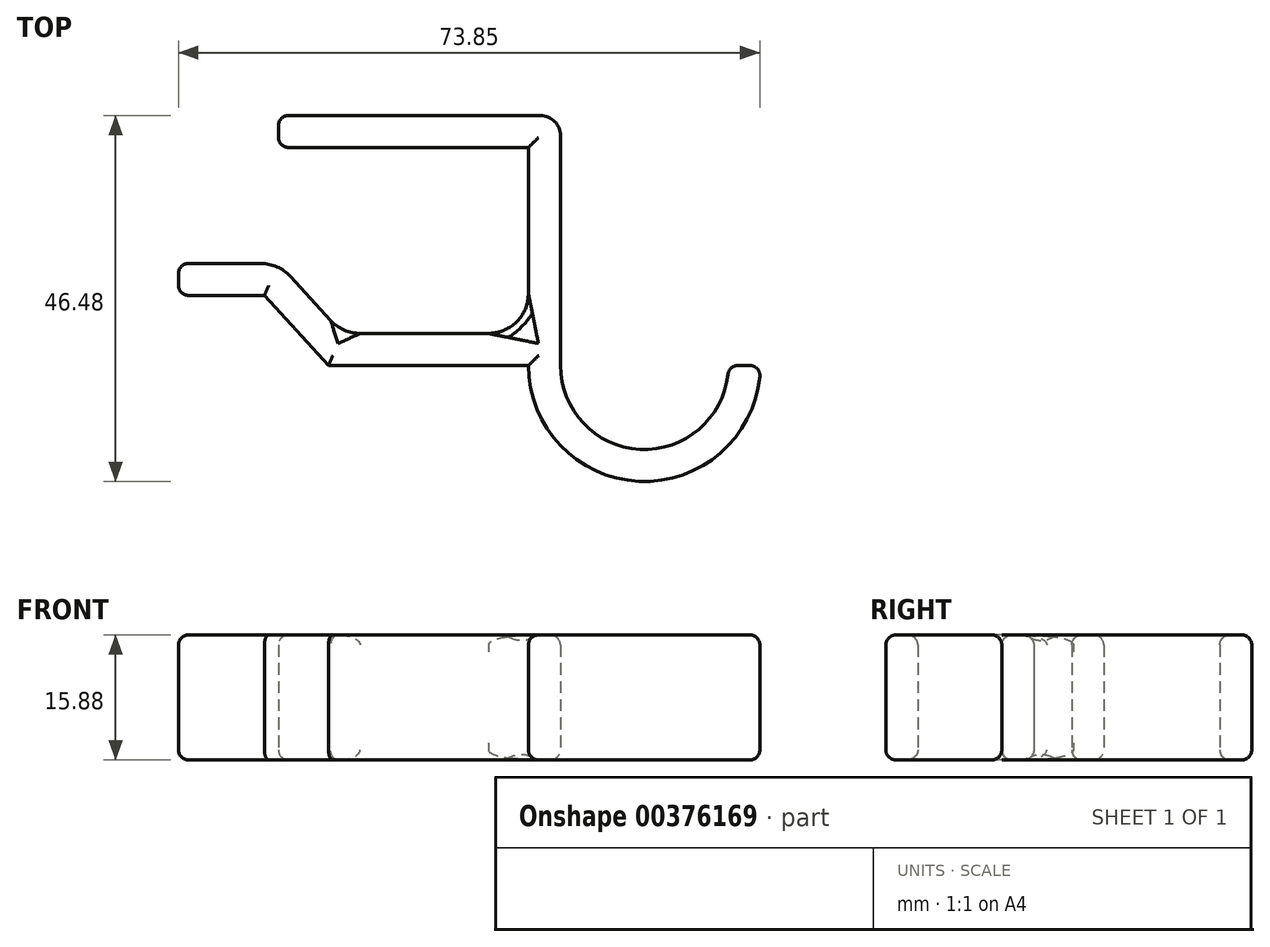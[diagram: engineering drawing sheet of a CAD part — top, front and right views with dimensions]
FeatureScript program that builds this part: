
annotation { "Feature Type Name" : "Feature", "Feature Type Description" : "" }
export const myFeature = defineFeature(function(context is Context, id is Id, definition is map)
    precondition{}
    {
        {
            var Q0;
            Q0=qCreatedBy(makeId("Top.planeOp"),FACE);
            var sketch = newSketch(context, id + "F0", { "sketchPlane" : qUnion([Q0])});
            skLineSegment(sketch, "E0", {"start": v(0, 0) * mm, "end": v(-31.75, 0) * mm});
            skLineSegment(sketch, "E1", {"start": v(-31.75, 0) * mm, "end": v(-31.75, 4.06) * mm});
            skLineSegment(sketch, "E2", {"start": v(-31.75, 4.06) * mm, "end": v(4.06, 4.06) * mm});
            skLineSegment(sketch, "E3", {"start": v(4.06, 4.06) * mm, "end": v(4.06, -27.69) * mm});
            skLineSegment(sketch, "E4", {"start": v(0, -27.69) * mm, "end": v(-25.4, -27.69) * mm});
            skLineSegment(sketch, "E5", {"start": v(-25.4, -27.69) * mm, "end": v(-33.54, -18.8) * mm});
            skLineSegment(sketch, "E6", {"start": v(-33.54, -18.8) * mm, "end": v(-44.45, -18.8) * mm});
            skLineSegment(sketch, "E7", {"start": v(-44.45, -18.8) * mm, "end": v(-44.45, -14.73) * mm});
            skLineSegment(sketch, "E8", {"start": v(-44.45, -14.73) * mm, "end": v(-31.75, -14.73) * mm});
            skLineSegment(sketch, "E9", {"start": v(-31.75, -14.73) * mm, "end": v(-23.61, -23.62) * mm});
            skLineSegment(sketch, "E10", {"start": v(-23.61, -23.62) * mm, "end": v(0, -23.62) * mm});
            skLineSegment(sketch, "E11", {"start": v(0, -23.62) * mm, "end": v(0, 0) * mm});
            skArc(sketch, "E12", {"start": v(4.06, -27.69) * mm, "mid": v(14.73, -38.35) * mm, "end": v(25.4, -27.69) * mm});
            skArc(sketch, "E13", {"start": v(0, -27.69) * mm, "mid": v(14.73, -42.42) * mm, "end": v(29.46, -27.69) * mm});
            skLineSegment(sketch, "E14", {"start": v(25.4, -27.69) * mm, "end": v(29.46, -27.69) * mm});
            skSolve(sketch);
        }
        {
            var Q0;
            Q0 = qSketchRegion(id + "F0", true);
            extrude(context, id + "F1", {"entities" : qUnion([Q0]), "depth" : 15.88 * mm});
        }
        {
            var Q0;
            Q0=makeQuery(id+"F1.opExtrude","SWEPT_EDGE",EDGE,{"disambiguationData":[OSD([sQuery(id+"F0.wireOp",EDGE,"E13"),sQuery(id+"F0.wireOp",EDGE,"E14")])]});
            var Q1;
            Q1=makeQuery(id+"F1.opExtrude","SWEPT_EDGE",EDGE,{"disambiguationData":[OSD([sQuery(id+"F0.wireOp",EDGE,"E12"),sQuery(id+"F0.wireOp",EDGE,"E14")])]});
            var Q2;
            Q2=makeQuery(id+"F1.opExtrude","CAP_EDGE",EDGE,{"disambiguationData":[OSD([sQuery(id+"F0.wireOp",EDGE,"E3")])],"isStart":false});
            var Q3;
            Q3=makeQuery(id+"F1.opExtrude","CAP_EDGE",EDGE,{"disambiguationData":[OSD([sQuery(id+"F0.wireOp",EDGE,"E2")])],"isStart":false});
            var Q4;
            Q4=makeQuery(id+"F1.opExtrude","CAP_FACE",FACE,{"disambiguationData":[OSD([sQuery(id+"F0.wireOp",EDGE,"E0"),sQuery(id+"F0.wireOp",EDGE,"E1"),sQuery(id+"F0.wireOp",EDGE,"E2"),sQuery(id+"F0.wireOp",EDGE,"E3"),sQuery(id+"F0.wireOp",EDGE,"E4"),sQuery(id+"F0.wireOp",EDGE,"E5"),sQuery(id+"F0.wireOp",EDGE,"E6"),sQuery(id+"F0.wireOp",EDGE,"E7"),sQuery(id+"F0.wireOp",EDGE,"E8"),sQuery(id+"F0.wireOp",EDGE,"E9"),sQuery(id+"F0.wireOp",EDGE,"E10"),sQuery(id+"F0.wireOp",EDGE,"E11"),sQuery(id+"F0.wireOp",EDGE,"E12"),sQuery(id+"F0.wireOp",EDGE,"E13"),sQuery(id+"F0.wireOp",EDGE,"E14")])],"isStart":false});
            var Q5;
            Q5=makeQuery(id+"F1.opExtrude","CAP_FACE",FACE,{"disambiguationData":[OSD([sQuery(id+"F0.wireOp",EDGE,"E0"),sQuery(id+"F0.wireOp",EDGE,"E1"),sQuery(id+"F0.wireOp",EDGE,"E2"),sQuery(id+"F0.wireOp",EDGE,"E3"),sQuery(id+"F0.wireOp",EDGE,"E4"),sQuery(id+"F0.wireOp",EDGE,"E5"),sQuery(id+"F0.wireOp",EDGE,"E6"),sQuery(id+"F0.wireOp",EDGE,"E7"),sQuery(id+"F0.wireOp",EDGE,"E8"),sQuery(id+"F0.wireOp",EDGE,"E9"),sQuery(id+"F0.wireOp",EDGE,"E10"),sQuery(id+"F0.wireOp",EDGE,"E11"),sQuery(id+"F0.wireOp",EDGE,"E12"),sQuery(id+"F0.wireOp",EDGE,"E13"),sQuery(id+"F0.wireOp",EDGE,"E14")])],"isStart":true});
            var Q6;
            Q6=makeQuery(id+"F1.opExtrude","SWEPT_EDGE",EDGE,{"disambiguationData":[OSD([sQuery(id+"F0.wireOp",EDGE,"E1"),sQuery(id+"F0.wireOp",EDGE,"E2")])]});
            var Q7;
            Q7=makeQuery(id+"F1.opExtrude","SWEPT_EDGE",EDGE,{"disambiguationData":[OSD([sQuery(id+"F0.wireOp",EDGE,"E0"),sQuery(id+"F0.wireOp",EDGE,"E1")])]});
            var Q8;
            Q8=makeQuery(id+"F1.opExtrude","CAP_EDGE",EDGE,{"disambiguationData":[OSD([sQuery(id+"F0.wireOp",EDGE,"E6")])],"isStart":true});
            var Q9;
            Q9=makeQuery(id+"F1.opExtrude","SWEPT_EDGE",EDGE,{"disambiguationData":[OSD([sQuery(id+"F0.wireOp",EDGE,"E7"),sQuery(id+"F0.wireOp",EDGE,"E8")])]});
            var Q10;
            Q10=makeQuery(id+"F1.opExtrude","SWEPT_EDGE",EDGE,{"disambiguationData":[OSD([sQuery(id+"F0.wireOp",EDGE,"E6"),sQuery(id+"F0.wireOp",EDGE,"E7")])]});
            fillet(context, id + "F2", {"entities" : qUnion([Q0, Q1, Q2, Q3, Q4, Q5, Q6, Q7, Q8, Q9, Q10]), "radius" : 1.27 * mm, "tangentPropagation" : true, "allowEdgeOverflow" : false});
        }
        {
            var Q0;
            Q0=makeQuery(id+"F1.opExtrude","SWEPT_EDGE",EDGE,{"disambiguationData":[OSD([sQuery(id+"F0.wireOp",EDGE,"E2"),sQuery(id+"F0.wireOp",EDGE,"E3")])]});
            fillet(context, id + "F3", {"entities" : qUnion([Q0]), "radius" : 2.54 * mm, "tangentPropagation" : true, "allowEdgeOverflow" : false});
        }
        {
            var Q0;
            Q0=makeQuery(id+"F1.opExtrude","SWEPT_EDGE",EDGE,{"disambiguationData":[OSD([sQuery(id+"F0.wireOp",EDGE,"E10"),sQuery(id+"F0.wireOp",EDGE,"E11")])]});
            var Q1;
            Q1=makeQuery(id+"F1.opExtrude","SWEPT_EDGE",EDGE,{"disambiguationData":[OSD([sQuery(id+"F0.wireOp",EDGE,"E9"),sQuery(id+"F0.wireOp",EDGE,"E10")])]});
            var Q2;
            Q2=makeQuery(id+"F1.opExtrude","SWEPT_EDGE",EDGE,{"disambiguationData":[OSD([sQuery(id+"F0.wireOp",EDGE,"E8"),sQuery(id+"F0.wireOp",EDGE,"E9")])]});
            fillet(context, id + "F4", {"entities" : qUnion([Q0, Q1, Q2]), "radius" : 5.08 * mm, "tangentPropagation" : true, "allowEdgeOverflow" : false});
        }
    });
